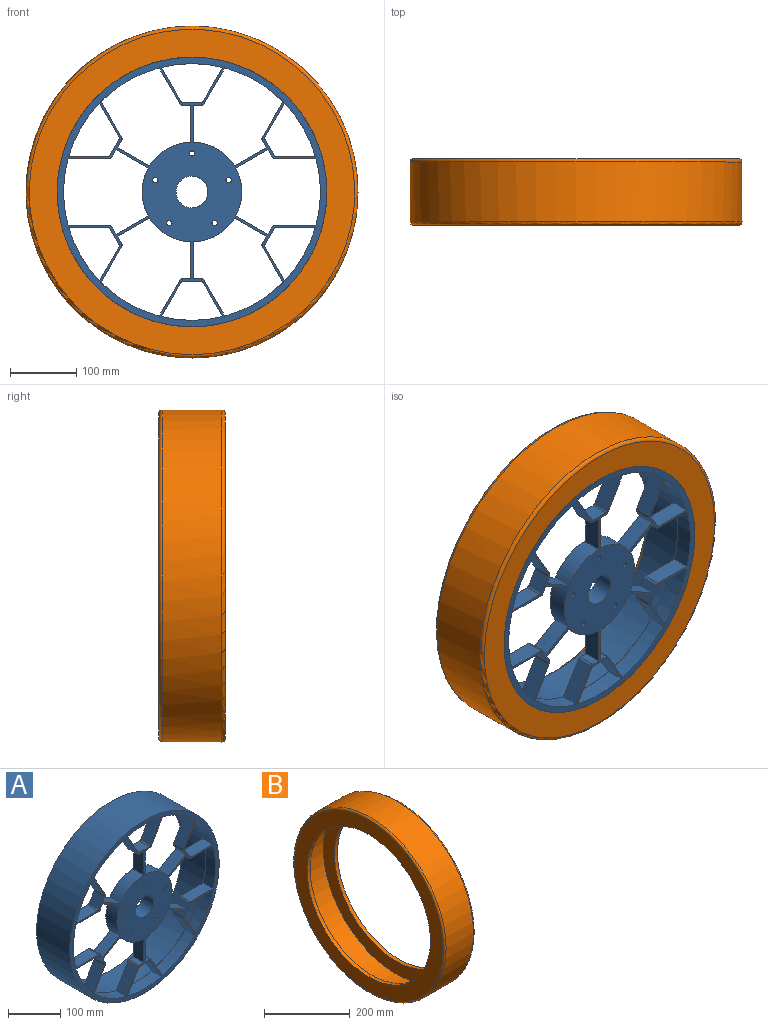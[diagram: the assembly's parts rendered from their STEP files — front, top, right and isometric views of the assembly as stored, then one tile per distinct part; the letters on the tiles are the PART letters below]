
ASSEMBLY  parts=2 mates=1
PART A: 103 faces, bbox 406.4x90x406.4 mm
  f0: plane 55.75x27mm, normal (-1,0,0), area 1505.1mm2, adj f17,f91,f96,f97
  f1: plane 48.28x27.87mm, normal (0.5,0,0.87), area 1505.1mm2, adj f18,f91,f96,f97
  f2: plane 48.28x27.87mm, normal (-0.5,0,0.87), area 1505.1mm2, adj f20,f91,f96,f97
  f3: plane 55.75x27mm, normal (1,0,0), area 1505.1mm2, adj f21,f91,f96,f97
  f4: plane 48.28x27.87mm, normal (-0.5,0,-0.87), area 1505.1mm2, adj f27,f91,f96,f97
  f5: plane 48.28x27.87mm, normal (-0.5,0,0.87), area 1505.1mm2, adj f28,f91,f96,f97
  f6: plane 48.28x27.87mm, normal (0.5,0,0.87), area 1505.1mm2, adj f34,f91,f96,f97
  f7: plane 48.28x27.87mm, normal (0.5,0,-0.87), area 1505.1mm2, adj f35,f91,f96,f97
  f8: plane 55.75x27mm, normal (1,0,0), area 1505.1mm2, adj f41,f91,f96,f97
  f9: plane 48.28x27.87mm, normal (-0.5,0,-0.87), area 1505.1mm2, adj f42,f91,f96,f97
  f10: plane 48.28x27.87mm, normal (0.5,0,-0.87), area 1505.1mm2, adj f48,f91,f96,f97
  f11: plane 55.75x27mm, normal (-1,0,0), area 1505.1mm2, adj f49,f91,f96,f97
  f12: cylinder r=4mm len=27mm, axis (0,-1,0), area 113.1mm2, adj f13,f18,f91,f96
  f13: plane 54.11x31.24mm, normal (0.87,0,0.5), area 1687.1mm2, adj f12,f14,f91,f96
  f14: cylinder r=193.25mm len=87.71mm, axis (0,-1,0), area 2766.7mm2, adj f13,f15,f91,f96
  f15: plane 54.11x31.24mm, normal (-0.87,0,-0.5), area 1687.1mm2, adj f14,f16,f91,f96
  f16: cylinder r=4mm len=27mm, axis (0,-1,0), area 113.1mm2, adj f15,f17,f91,f96
  f17: plane 27x12.69mm, normal (0,0,-1), area 342.6mm2, adj f0,f16,f91,f96
  f18: plane 27x10.99mm, normal (0.87,0,-0.5), area 342.6mm2, adj f1,f12,f91,f96
  f19: cylinder r=4mm len=27mm, axis (0,-1,0), area 113.1mm2, adj f20,f25,f91,f96
  f20: plane 27x10.99mm, normal (-0.87,0,-0.5), area 342.6mm2, adj f2,f19,f91,f96
  f21: plane 27x12.69mm, normal (0,0,-1), area 342.6mm2, adj f3,f22,f91,f96
  f22: cylinder r=4mm len=27mm, axis (0,-1,0), area 113.1mm2, adj f21,f23,f91,f96
  f23: plane 54.11x31.24mm, normal (0.87,0,-0.5), area 1687.1mm2, adj f22,f24,f91,f96
  f24: cylinder r=193.25mm len=87.71mm, axis (0,-1,0), area 2766.7mm2, adj f23,f25,f91,f96
  f25: plane 54.11x31.24mm, normal (-0.87,0,0.5), area 1687.1mm2, adj f19,f24,f91,f96
  f26: cylinder r=4mm len=27mm, axis (0,-1,0), area 113.1mm2, adj f27,f32,f91,f96
  f27: plane 27x10.99mm, normal (0.87,0,-0.5), area 342.6mm2, adj f4,f26,f91,f96
  f28: plane 27x10.99mm, normal (0.87,0,0.5), area 342.6mm2, adj f5,f29,f91,f96
  f29: cylinder r=4mm len=27mm, axis (0,-1,0), area 113.1mm2, adj f28,f30,f91,f96
  f30: plane 62.49x27mm, normal (0,0,1), area 1687.1mm2, adj f29,f31,f91,f96
  f31: cylinder r=193.25mm len=101.27mm, axis (0,-1,0), area 2766.7mm2, adj f30,f32,f91,f96
  f32: plane 62.49x27mm, normal (0,0,-1), area 1687.1mm2, adj f26,f31,f91,f96
  f33: cylinder r=4mm len=27mm, axis (0,-1,0), area 113.1mm2, adj f34,f39,f91,f96
  f34: plane 27x10.99mm, normal (-0.87,0,0.5), area 342.6mm2, adj f6,f33,f91,f96
  f35: plane 27x10.99mm, normal (-0.87,0,-0.5), area 342.6mm2, adj f7,f36,f91,f96
  f36: cylinder r=4mm len=27mm, axis (0,-1,0), area 113.1mm2, adj f35,f37,f91,f96
  f37: plane 62.49x27mm, normal (0,0,-1), area 1687.1mm2, adj f36,f38,f91,f96
  f38: cylinder r=193.25mm len=101.27mm, axis (0,-1,0), area 2766.7mm2, adj f37,f39,f91,f96
  f39: plane 62.49x27mm, normal (0,0,1), area 1687.1mm2, adj f33,f38,f91,f96
  f40: cylinder r=4mm len=27mm, axis (0,-1,0), area 113.1mm2, adj f41,f46,f91,f96
  f41: plane 27x12.69mm, normal (0,0,1), area 342.6mm2, adj f8,f40,f91,f96
  f42: plane 27x10.99mm, normal (-0.87,0,0.5), area 342.6mm2, adj f9,f43,f91,f96
  f43: cylinder r=4mm len=27mm, axis (0,-1,0), area 113.1mm2, adj f42,f44,f91,f96
  f44: plane 54.11x31.24mm, normal (-0.87,0,-0.5), area 1687.1mm2, adj f43,f45,f91,f96
  f45: cylinder r=193.25mm len=87.71mm, axis (0,-1,0), area 2766.7mm2, adj f44,f46,f91,f96
  f46: plane 54.11x31.24mm, normal (0.87,0,0.5), area 1687.1mm2, adj f40,f45,f91,f96
  f47: cylinder r=4mm len=27mm, axis (0,-1,0), area 113.1mm2, adj f48,f53,f91,f96
  f48: plane 27x10.99mm, normal (0.87,0,0.5), area 342.6mm2, adj f10,f47,f91,f96
  f49: plane 27x12.69mm, normal (0,0,1), area 342.6mm2, adj f11,f50,f91,f96
  f50: cylinder r=4mm len=27mm, axis (0,-1,0), area 113.1mm2, adj f49,f51,f91,f96
  f51: plane 54.11x31.24mm, normal (-0.87,0,0.5), area 1687.1mm2, adj f50,f52,f91,f96
  f52: cylinder r=193.25mm len=87.71mm, axis (0,-1,0), area 2766.7mm2, adj f51,f53,f91,f96
  f53: plane 54.11x31.24mm, normal (0.87,0,-0.5), area 1687.1mm2, adj f47,f52,f91,f96
  f54: cylinder r=193.25mm len=92.37mm, axis (0,-1,0), area 2518.4mm2, adj f55,f59,f91,f96
  f55: plane 50.93x29.41mm, normal (-0.87,0,0.5), area 1587.9mm2, adj f54,f56,f91,f96
  f56: cylinder r=4mm len=27mm, axis (0,-1,0), area 113.1mm2, adj f55,f57,f91,f96
  f57: plane 27x26.63mm, normal (0,0,1), area 719mm2, adj f56,f58,f91,f96
  f58: cylinder r=4mm len=27mm, axis (0,-1,0), area 113.1mm2, adj f57,f59,f91,f96
  f59: plane 50.93x29.41mm, normal (0.87,0,0.5), area 1587.9mm2, adj f54,f58,f91,f96
  f60: plane 58.81x27mm, normal (0,0,1), area 1587.9mm2, adj f61,f65,f91,f96
  f61: cylinder r=193.25mm len=80mm, axis (0,-1,0), area 2518.4mm2, adj f60,f62,f91,f96
  f62: plane 50.93x29.41mm, normal (-0.87,0,-0.5), area 1587.9mm2, adj f61,f63,f91,f96
  f63: cylinder r=4mm len=27mm, axis (0,-1,0), area 113.1mm2, adj f62,f64,f91,f96
  f64: plane 27x23.06mm, normal (-0.87,0,0.5), area 719mm2, adj f63,f65,f91,f96
  f65: cylinder r=4mm len=27mm, axis (0,-1,0), area 113.1mm2, adj f60,f64,f91,f96
  f66: plane 50.93x29.41mm, normal (-0.87,0,0.5), area 1587.9mm2, adj f67,f71,f91,f96
  f67: cylinder r=193.25mm len=80mm, axis (0,-1,0), area 2518.4mm2, adj f66,f68,f91,f96
  f68: plane 58.81x27mm, normal (0,0,-1), area 1587.9mm2, adj f67,f69,f91,f96
  f69: cylinder r=4mm len=27mm, axis (0,-1,0), area 113.1mm2, adj f68,f70,f91,f96
  f70: plane 27x23.06mm, normal (-0.87,0,-0.5), area 719mm2, adj f69,f71,f91,f96
  f71: cylinder r=4mm len=27mm, axis (0,-1,0), area 113.1mm2, adj f66,f70,f91,f96
  f72: plane 50.93x29.41mm, normal (-0.87,0,-0.5), area 1587.9mm2, adj f73,f77,f91,f96
  f73: cylinder r=193.25mm len=92.37mm, axis (0,-1,0), area 2518.4mm2, adj f72,f74,f91,f96
  f74: plane 50.93x29.41mm, normal (0.87,0,-0.5), area 1587.9mm2, adj f73,f75,f91,f96
  f75: cylinder r=4mm len=27mm, axis (0,-1,0), area 113.1mm2, adj f74,f76,f91,f96
  f76: plane 27x26.63mm, normal (0,0,-1), area 719mm2, adj f75,f77,f91,f96
  f77: cylinder r=4mm len=27mm, axis (0,-1,0), area 113.1mm2, adj f72,f76,f91,f96
  f78: plane 58.81x27mm, normal (0,0,-1), area 1587.9mm2, adj f79,f83,f91,f96
  f79: cylinder r=193.25mm len=80mm, axis (0,-1,0), area 2518.4mm2, adj f78,f80,f91,f96
  f80: plane 50.93x29.41mm, normal (0.87,0,0.5), area 1587.9mm2, adj f79,f81,f91,f96
  f81: cylinder r=4mm len=27mm, axis (0,-1,0), area 113.1mm2, adj f80,f82,f91,f96
  f82: plane 27x23.06mm, normal (0.87,0,-0.5), area 719mm2, adj f81,f83,f91,f96
  f83: cylinder r=4mm len=27mm, axis (0,-1,0), area 113.1mm2, adj f78,f82,f91,f96
  f84: plane 50.93x29.41mm, normal (0.87,0,-0.5), area 1587.9mm2, adj f85,f89,f91,f96
  f85: cylinder r=193.25mm len=80mm, axis (0,-1,0), area 2518.4mm2, adj f84,f86,f91,f96
  f86: plane 58.81x27mm, normal (0,0,1), area 1587.9mm2, adj f85,f87,f91,f96
  f87: cylinder r=4mm len=27mm, axis (0,-1,0), area 113.1mm2, adj f86,f88,f91,f96
  f88: plane 27x23.06mm, normal (0.87,0,0.5), area 719mm2, adj f87,f89,f91,f96
  f89: cylinder r=4mm len=27mm, axis (0,-1,0), area 113.1mm2, adj f84,f88,f91,f96
  f90: plane 150x150mm, normal (0,1,0), area 15610.6mm2, adj f95,f97,f98,f99,f100,f101,f102
  f91: plane 406.4x406.4mm, normal (0,-1,0), area 32532.1mm2, adj f0,f1,f2,f3,f4,f5,f6,f7
  f92: plane 406.4x406.4mm, normal (0,1,0), area 11797.1mm2, adj f93,f94
  f93: cylinder r=203.2mm len=406.4mm, axis (0,1,0), area 114906.9mm2, adj f91,f92
  f94: cylinder r=193.74mm len=387.48mm, axis (0,-1,0), area 76690.1mm2, adj f92,f96
  f95: cylinder r=24mm len=48mm, axis (0,1,0), area 4523.9mm2, adj f90,f91
  f96: plane 387.48x387.48mm, normal (0,1,0), area 5124.4mm2, adj f0,f1,f2,f3,f4,f5,f6,f7
  f97: cylinder r=75mm len=150mm, axis (0,-1,0), area 13489.1mm2, adj f0,f1,f2,f3,f4,f5,f6,f7
  f98: cylinder r=4mm len=30mm, axis (0,-1,0), area 754mm2, adj f90,f91
  f99: cylinder r=4mm len=30mm, axis (0,-1,0), area 754mm2, adj f90,f91
  f100: cylinder r=4mm len=30mm, axis (0,-1,0), area 754mm2, adj f90,f91
  f101: cylinder r=4mm len=30mm, axis (0,-1,0), area 754mm2, adj f90,f91
  f102: cylinder r=4mm len=30mm, axis (0,-1,0), area 754mm2, adj f90,f91
PART B: 10 faces, bbox 100x541.2x541.2 mm
  f0: plane 490x490mm, normal (1,0,0), area 58857mm2, adj f7,f9
  f1: cylinder r=250mm len=500mm, axis (-1,0,0), area 141371.7mm2, adj f8,f9
  f2: plane 490x490mm, normal (-1,0,0), area 58857mm2, adj f3,f8
  f3: cylinder r=203.2mm len=406.4mm, axis (-1,0,0), area 12767.4mm2, adj f2,f4
  f4: plane 480x480mm, normal (1,0,0), area 51238.6mm2, adj f3,f5
  f5: cylinder r=240mm len=480mm, axis (-1,0,0), area 120637.2mm2, adj f4,f6
  f6: plane 480x480mm, normal (-1,0,0), area 51238.6mm2, adj f5,f7
  f7: cylinder r=203.2mm len=406.4mm, axis (-1,0,0), area 12767.4mm2, adj f0,f6
  f8: torus R=245mm, axis (-1,0,0), area 12247.3mm2, adj f1,f2
  f9: torus R=245mm, axis (1,0,0), area 12247.3mm2, adj f0,f1
PLACE A t=(-2.14,56.17,-9.27)mm
PLACE B rot(axis=(-0.58,0.58,-0.58),120deg) t=(-2.14,-205.86,-9.27)mm
MATE fastened B.f1 <-> A.f14  axis (0,-1,0) through (-2.14,-33.83,-9.27)mm
